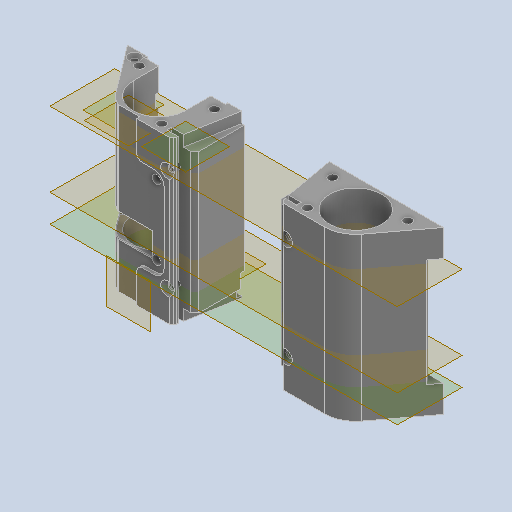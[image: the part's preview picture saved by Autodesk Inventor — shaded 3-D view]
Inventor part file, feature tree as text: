
AUTODESK INVENTOR PART (.ipt)
format: ipt  version: 2022 (Build 260153000, 153)  size: 1,885,696 bytes
history: native  units: mm
features: sketch x43, reference x43, extrude x42, fillet x40, projected_geometry x36, other x34, chamfer x5, mirror x2
ambient origin geometry x8: Origin, YZ Plane, XZ Plane, XY Plane, X Axis, Y Axis, Z Axis, Center Point
bodies: Body1 (feature_tree)
feature tree (245):
  other  "Твердое тело1"
  extrude  "Выдавливание1"  Depth=3.0mm
  extrude  "Выдавливание3"  Depth=3.0mm
  other  "РабПлоскость3"
  extrude  "Выдавливание4"  Depth=0.5mm
  other  "РабПлоскость6"
  extrude  "Выдавливание5"  Depth=0.5mm
  other  "РабПлоскость2"
  extrude  "Выдавливание6"  Depth=150.0mm
  fillet  "Сопряжение1"  Radius=81.0mm
  extrude  "Выдавливание7"  Depth=14.0mm TaperAngle=0.0deg
  chamfer  "Фаска2"  Distance=14.0mm
  extrude  "Выдавливание8"  Depth=2.0mm
  mirror  "Зеркальное отражение2"
  sketch  "Эскиз11"
  extrude  "Выдавливание10"  Depth=2.0mm
  extrude  "Выдавливание11"  TaperAngle=0.0deg  [1 undecoded]
  extrude  "Выдавливание12"  Depth=2.0mm
  extrude  "Выдавливание13"  Depth=65.0mm
  extrude  "Выдавливание14"  Depth=2.2mm
  extrude  "Выдавливание15"  Depth=10.0mm TaperAngle=0.0deg
  extrude  "Выдавливание16"  Depth=300.0mm TaperAngle=0.0deg
  extrude  "Выдавливание17"  Depth=41.5mm
  fillet  "Сопряжение2"  Radius=81.0mm
  fillet  "Сопряжение3"  Radius=30.0mm
  fillet  "Сопряжение4"  Radius=30.0mm
  sketch  "Эскиз21"
  extrude  "Выдавливание21"  Depth=2.0mm
  fillet  "Сопряжение7"  Radius=3.0mm
  other  "РабПлоскость7"
  extrude  "Выдавливание22"  Depth=15.0mm
  extrude  "Выдавливание23"  Depth=15.0mm
  other  "РабПлоскость8"
  extrude  "Выдавливание24"  Depth=3.2mm
  mirror  "Зеркальное отражение6"
  chamfer  "Фаска4"  Distance=3.2mm
  fillet  "Сопряжение9"  Radius=50.0mm
  extrude  "Выдавливание31"  Depth=2.0mm TaperAngle=45.0deg
  chamfer  "Фаска5"  Distance=4.2mm
  other  "РабПлоскость13"
  other  "РабПлоскость11"
  extrude  "Выдавливание35"  Depth=4.0mm
  extrude  "Выдавливание36"  Depth=4.0mm
  extrude  "Выдавливание37"  Depth=6.0mm TaperAngle=0.0deg
  other  "РабПлоскость12"
  extrude  "Выдавливание38"  Depth=4.2mm
  extrude  "Выдавливание39"  Depth=4.2mm
  fillet  "Сопряжение14"  Radius=4.2mm
  fillet  "Сопряжение15"  Radius=4.2mm
  fillet  "Сопряжение16"  Radius=8.0mm
  extrude  "Выдавливание40"  Depth=4.2mm
  extrude  "Выдавливание41"  Depth=4.2mm
  extrude  "Выдавливание42"  Depth=8.0mm TaperAngle=0.0deg
  fillet  "Сопряжение17"  Radius=35.0mm
  fillet  "Сопряжение18"  Radius=4.2mm
  extrude  "Выдавливание43"  Depth=4.2mm
  fillet  "Сопряжение19"  Radius=6.0mm
  fillet  "Сопряжение20"  Radius=20.0mm
  fillet  "Сопряжение21"  Radius=10.0mm
  fillet  "Сопряжение22"  Radius=1.5mm
  extrude  "Выдавливание44"  Depth=0.3mm
  extrude  "Выдавливание45"  Depth=0.3mm
  fillet  "Сопряжение23"  Radius=0.3mm
  fillet  "Сопряжение24"  Radius=8.5mm
  extrude  "Выдавливание46"  Depth=4.95mm
  fillet  "Сопряжение25"  Radius=0.3mm
  other  "РабПлоскость14"
  extrude  "Выдавливание47"  Depth=2.0mm
  fillet  "Сопряжение26"  Radius=3.0mm
  extrude  "Выдавливание48"  Depth=25.0mm
  fillet  "Сопряжение27"  Radius=1.0mm
  extrude  "Выдавливание49"  Depth=0.5mm
  chamfer  "Фаска6"  Distance=0.5mm
  fillet  "Сопряжение28"  Radius=25.0mm
  fillet  "Сопряжение29"  Radius=1.7mm
  extrude  "Выдавливание50"  Depth=35.0mm TaperAngle=0.0deg
  fillet  "Сопряжение30"  Radius=11.0mm
  fillet  "Сопряжение31"  Radius=35.0mm
  fillet  "Сопряжение32"  Radius=12.0mm
  extrude  "Выдавливание51"  Depth=0.3mm
  fillet  "Сопряжение33"  Radius=1.0mm
  extrude  "Выдавливание52"  Depth=1.0mm
  fillet  "Сопряжение36"  Radius=2.0mm
  fillet  "Сопряжение37"  Radius=0.5mm
  fillet  "Сопряжение39"  [1 undecoded]
  fillet  "Сопряжение40"  Radius=3.2mm
  fillet  "Сопряжение41"  Radius=1.0mm
  extrude  "Выдавливание53"  Depth=7.0mm
  fillet  "Сопряжение42"  Radius=0.5mm
  extrude  "Выдавливание54"  Depth=0.5mm TaperAngle=0.0deg
  fillet  "Сопряжение43"  Radius=3.1mm
  extrude  "Выдавливание55"  Depth=20.0mm TaperAngle=0.0deg
  fillet  "Сопряжение44"  Radius=1.0mm
  other  "РабПлоскость15"
  fillet  "Сопряжение45"  Radius=3.0mm
  chamfer  "Фаска7"  Distance=2.0mm Angle=45.0deg
  fillet  "Сопряжение46"  Radius=0.5mm
  fillet  "Сопряжение47"  Radius=0.6mm
  fillet  "Сопряжение48"  Radius=0.6mm
  fillet  "Сопряжение49"  Radius=70.0mm
  fillet  "Сопряжение50"  Radius=2.0mm
  extrude  "Выдавливание56"  Depth=7.0mm TaperAngle=0.0deg
  sketch  "Эскиз1"
  reference  "Ссылка1"
  reference  "Ссылка2"
  reference  "Ссылка3"
  reference  "Ссылка4"
  reference  "Ссылка5"
  reference  "Ссылка6"
  reference  "Ссылка7"
  reference  "Ссылка8"
  reference  "Ссылка9"
  sketch  "Эскиз4"
  sketch  "Эскиз5"
  sketch  "Эскиз6"
  sketch  "Эскиз7"
  projected_geometry  "Спроецированная петля5"
  projected_geometry  "Спроецированная петля6"
  sketch  "Эскиз8"
  reference  "Ссылка17"
  projected_geometry  "Спроецированная петля7"
  sketch  "Эскиз9"
  reference  "Ссылка18"
  reference  "Ссылка19"
  reference  "Ссылка20"
  sketch  "Эскиз12"
  reference  "Ссылка23"
  sketch  "Эскиз13"
  sketch  "Эскиз15"
  projected_geometry  "Спроецированная петля13"
  sketch  "Эскиз16"
  projected_geometry  "Спроецированная петля14"
  projected_geometry  "Спроецированная петля15"
  projected_geometry  "Спроецированная петля16"
  sketch  "Эскиз17"
  reference  "Ссылка24"
  reference  "Ссылка25"
  sketch  "Эскиз18"
  projected_geometry  "Спроецированная петля19"
  sketch  "Эскиз19"
  projected_geometry  "Спроецированная петля20"
  sketch  "Эскиз20"
  projected_geometry  "Спроецированная петля21"
  projected_geometry  "Спроецированная петля22"
  projected_geometry  "Спроецированная петля23"
  projected_geometry  "Спроецированная петля24"
  sketch  "Эскиз25"
  reference  "Ссылка27"
  reference  "Ссылка28"
  reference  "Ссылка29"
  sketch  "Эскиз26"
  reference  "Ссылка30"
  reference  "Ссылка31"
  sketch  "Эскиз27"
  projected_geometry  "Спроецированная петля28"
  sketch  "Эскиз28"
  projected_geometry  "Спроецированная петля29"
  reference  "Ссылка32"
  reference  "Ссылка33"
  reference  "Ссылка34"
  other  "РабПлоскость9"
  sketch  "Эскиз36"
  projected_geometry  "Спроецированная петля37"
  projected_geometry  "Спроецированная петля38"
  reference  "Ссылка42"
  reference  "Ссылка43"
  sketch  "Эскиз39"
  reference  "Ссылка45"
  sketch  "Эскиз40"
  projected_geometry  "Спроецированная петля41"
  reference  "Ссылка46"
  reference  "Ссылка47"
  sketch  "Эскиз41"
  reference  "Ссылка48"
  reference  "Ссылка49"
  reference  "Ссылка50"
  sketch  "Эскиз42"
  reference  "Ссылка51"
  projected_geometry  "Спроецированная петля42"
  sketch  "Эскиз43"
  projected_geometry  "Спроецированная петля43"
  sketch  "Эскиз44"
  reference  "Ссылка52"
  sketch  "Эскиз45"
  reference  "Ссылка53"
  reference  "Ссылка54"
  sketch  "Эскиз46"
  projected_geometry  "Спроецированная петля44"
  sketch  "Эскиз47"
  projected_geometry  "Спроецированная петля45"
  projected_geometry  "Спроецированная петля46"
  sketch  "Эскиз48"
  projected_geometry  "Спроецированная петля47"
  sketch  "Эскиз49"
  sketch  "Эскиз50"
  projected_geometry  "Спроецированная петля48"
  projected_geometry  "Спроецированная петля49"
  projected_geometry  "Спроецированная петля50"
  sketch  "Эскиз52"
  projected_geometry  "Спроецированная петля51"
  sketch  "Эскиз53"
  projected_geometry  "Спроецированная петля52"
  projected_geometry  "Спроецированная петля53"
  reference  "Ссылка55"
  sketch  "Эскиз54"
  reference  "Ссылка56"
  reference  "Ссылка57"
  sketch  "Эскиз55"
  projected_geometry  "Спроецированная петля54"
  sketch  "Эскиз56"
  projected_geometry  "Спроецированная петля55"
  reference  "Ссылка58"
  sketch  "Эскиз57"
  projected_geometry  "Спроецированная петля56"
  projected_geometry  "Спроецированная петля57"
  sketch  "Эскиз58"
  projected_geometry  "Спроецированная петля58"
  sketch  "Эскиз59"
  projected_geometry  "Спроецированная петля59"
  sketch  "Эскиз60"
  reference  "Ссылка59"
  reference  "Ссылка60"
  reference  "Ссылка61"
  other  "<userpath>\Documents\Git\MZCAT_2024\MZCAT.iam"
  other  "MZCAT.iam"
  other  "plan:1"
  other  "akkum_plate:1"
  other  "main_wheel_fixator:1"
  other  "CAT_protector:1"
  other  "base plate:2"
  other  "<userpath>\Documents\Git\MZCAT_2024_construction\MZCAT_2024_RPI_2\MZCAT_4.iam"
  other  "MZCAT_4.iam"
  other  "OCS-D008 B:1"
  other  "Linit Switch:2"
  other  "Linit Switch:1"
  other  "concevik:1"
  other  "FastBattery:1"
  other  "metal_cap:1"
  other  "vydacha_slide:1"
  other  "motherboard_plate:1"
  other  "cable_slide2:1"
  other  "cable_slide:1"
  other  "upor:1"
  other  "usb_camera_board:1"
  other  "<userpath>\Documents\Git\MZCAT_2024\MZCAT_4.iam"
note: 2 required parameter values undecoded (feature->parameter linkage not recoverable at this tier; creation-order binding heuristic only, values carry confidence <= 0.55)
